FCSTD DOCUMENT  (FreeCAD 0.18.1R)
Label: Z_drive
License: All rights reserved
LicenseURL: http://en.wikipedia.org/wiki/All_rights_reserved
objects: App::FeaturePython×5, Part::Feature×2, App::Part×1, Part::Compound×1, Part::FeaturePython×1
note: 4 computed .brp shape members not serialized (recipe doc carries the construction recipe); baked Part::Feature solids carry a one-line shape summary decoded from their .brp

FEATURE [Part::Feature] Part__Feature001  label="Nema 17  Stepper Motor length 34mm"
  Placement = pos=(-9,-3.5006,1) rot=(0,1,0;1.5708rad)
  shape: bbox 61.3 x 57.6 x 42.3 mm, 990 faces, 27 solids (baked)
FEATURE [App::Part] Part
  Group = -> [Part__Feature001]
  Origin = -> Origin
FEATURE [Part::Compound] Compound
  Links = -> [Part__Feature001]
FEATURE [Part::Feature] Part__Feature  label="z_drive_rear_support_b_x2(Solid)"
  Placement = pos=(-119.829,35.8994,119.173) rot=(0.57735,0.57735,-0.57735;2.0944rad)
  shape: bbox 98.17 x 20 x 61.02 mm, 21513 faces (baked)
FEATURE [Part::FeaturePython] z_drive_front_support_b_x2_stp1_01  # a2plus imported part (geometry in sourceFile) (typed FeaturePython)
  Placement = pos=(-223,1.619e-13,-103) rot=(-0.57735,-0.57735,-0.57735;2.0944rad)
  fixedPosition = true
  sourceFile = <userpath>/_workspace/3d-printer-tryout/CAD/voron_parts_cad/VORON2.1/Z Drive/z_drive_front_support_b_x2.stp
  timeLastImport = 1.55522e+09
  updateColors = true
FEATURE [App::FeaturePython] planeConstraint01  # a2plus constraint (typed FeaturePython)
  Object1 = Part__Feature001
  Object2 = Part__Feature
  SubElement1 = Face159
  SubElement2 = Face4367
  Type = plane
  directionConstraint = 1
  offset = 0
FEATURE [App::FeaturePython] planeConstraint02  label="planeConstraint02__z_drive_rear_support_b_x2(Solid)"  # a2plus constraint (typed FeaturePython)
  Object1 = z_drive_front_support_b_x2_stp1_01
  Object2 = Part__Feature
  SubElement1 = Face29736
  SubElement2 = Face20243
  Type = plane
  directionConstraint = 0
  offset = 0
FEATURE [App::FeaturePython] planeConstraint02_mirror  label="planeConstraint02__z_drive_front_support_b_x2_stp1_01"  # a2plus constraint (typed FeaturePython)
  Object1 = z_drive_front_support_b_x2_stp1_01
  Object2 = Part__Feature
  SubElement1 = Face29736
  SubElement2 = Face20243
  Type = plane
  directionConstraint = 0
  offset = 0
FEATURE [App::FeaturePython] planeConstraint03  label="planeConstraint03__z_drive_rear_support_b_x2(Solid)"  # a2plus constraint (typed FeaturePython)
  Object1 = z_drive_front_support_b_x2_stp1_01
  Object2 = Part__Feature
  SubElement1 = Face30677
  SubElement2 = Face20616
  Type = plane
  directionConstraint = 0
  offset = 0
FEATURE [App::FeaturePython] planeConstraint03_mirror  label="planeConstraint03__z_drive_front_support_b_x2_stp1_01"  # a2plus constraint (typed FeaturePython)
  Object1 = z_drive_front_support_b_x2_stp1_01
  Object2 = Part__Feature
  SubElement1 = Face30677
  SubElement2 = Face20616
  Type = plane
  directionConstraint = 0
  offset = 0
